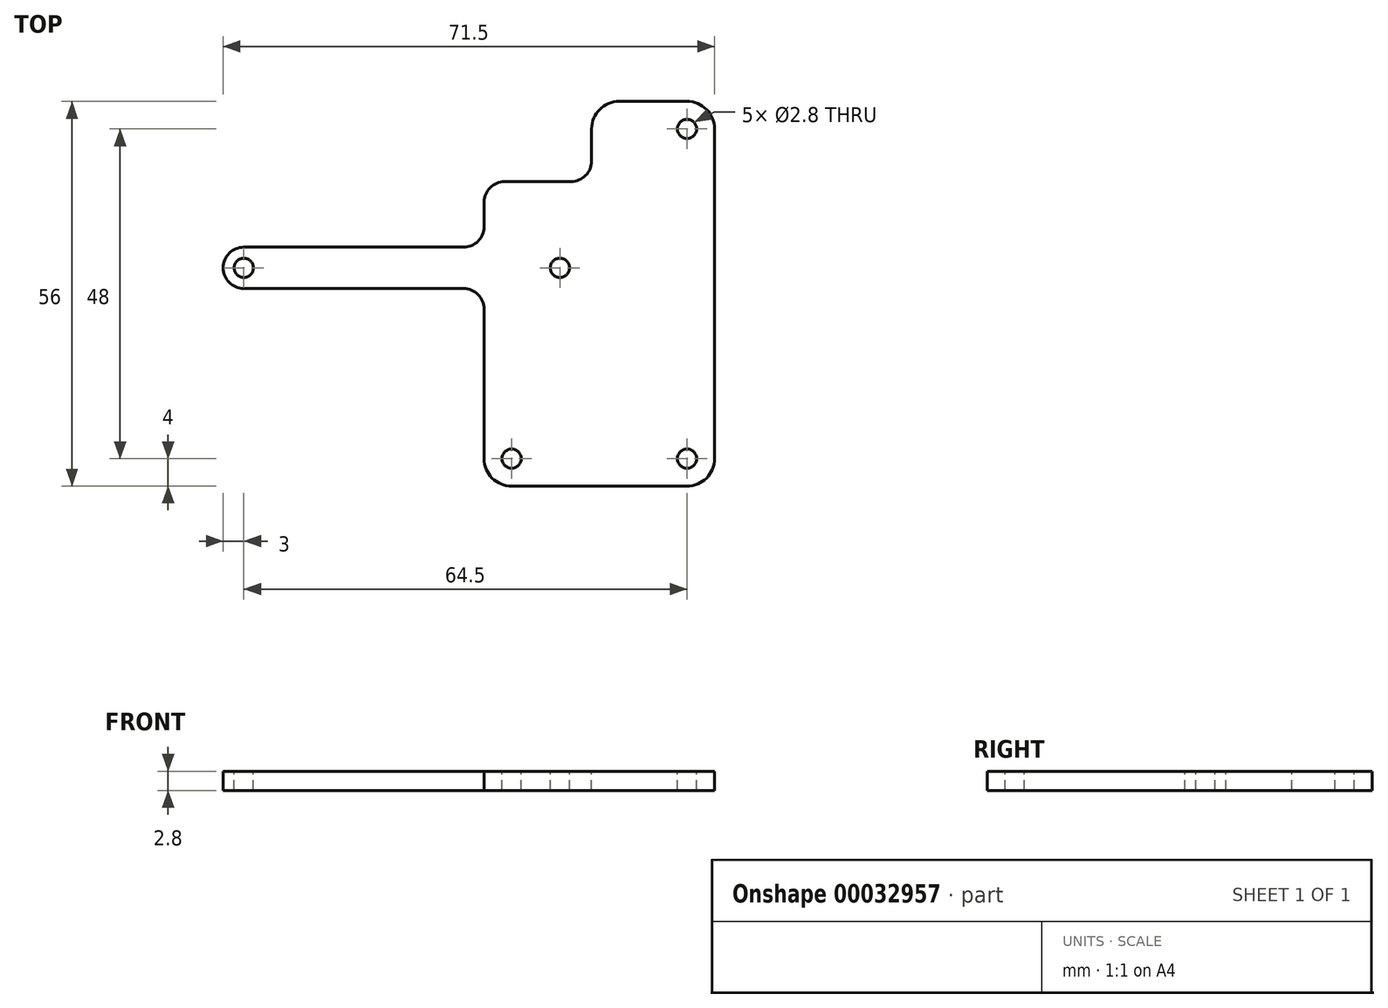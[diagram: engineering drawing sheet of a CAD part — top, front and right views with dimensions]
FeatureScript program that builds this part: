
annotation { "Feature Type Name" : "Feature", "Feature Type Description" : "" }
export const myFeature = defineFeature(function(context is Context, id is Id, definition is map)
    precondition{}
    {
        {
            var Q0;
            Q0=qCreatedBy(makeId("Top.planeOp"),FACE);
            var sketch = newSketch(context, id + "F0", { "sketchPlane" : qUnion([Q0])});
            skLineSegment(sketch, "E0.rect.bottom", {"start": v(5.82, -11.88) * mm, "end": v(-5.83, -11.88) * mm});
            skLineSegment(sketch, "E0.rect.top", {"start": v(5.83, 11.88) * mm, "end": v(-5.82, 11.88) * mm});
            skLineSegment(sketch, "E0.rect.left", {"start": v(5.82, -11.88) * mm, "end": v(5.83, 11.88) * mm});
            skLineSegment(sketch, "E0.rect.right", {"start": v(-5.83, -11.88) * mm, "end": v(-5.82, 11.87) * mm});
            skPoint(sketch, "E0.rect.middle", {"position": v(0, 0) * mm});
            skSolve(sketch);
        }
        {
            var Q0;
            Q0=qSketchRegion(id+"F0",true);
            extrude(context, id + "F1", {"entities" : qUnion([Q0]), "depth" : 20.4 * mm});
        }
        {
            var Q0;
            Q0=makeQuery(id+"F1.opExtrude","CAP_FACE",FACE,{"disambiguationData":[OSD([sQuery(id+"F0.wireOp",EDGE,"E0.rect.bottom"),sQuery(id+"F0.wireOp",EDGE,"E0.rect.top"),sQuery(id+"F0.wireOp",EDGE,"E0.rect.left"),sQuery(id+"F0.wireOp",EDGE,"E0.rect.right")])],"isStart":false});
            var sketch = newSketch(context, id + "F2", { "sketchPlane" : qUnion([Q0])});
            skArc(sketch, "E1", {"start": v(5.83, 7.59) * mm, "mid": v(0, 11.88) * mm, "end": v(-5.83, 7.59) * mm});
            skLineSegment(sketch, "E2", {"start": v(5.83, 7.59) * mm, "end": v(5.83, 3.96) * mm});
            skLineSegment(sketch, "E3.MirrorCS", {"start": v(-5.83, 7.59) * mm, "end": v(-5.83, 3.96) * mm});
            skArc(sketch, "E4.trimOffspring", {"start": v(-5.83, 3.96) * mm, "mid": v(-4.78, 1.98) * mm, "end": v(-3.09, 0.51) * mm});
            skArc(sketch, "E5", {"start": v(-3.09, 0.51) * mm, "mid": v(0, -3.1) * mm, "end": v(3.09, 0.51) * mm});
            skArc(sketch, "E6.trimOffspring", {"start": v(3.09, 0.51) * mm, "mid": v(4.78, 1.98) * mm, "end": v(5.83, 3.96) * mm});
            skSolve(sketch);
        }
        {
            var Q0;
            Q0=qSketchRegion(id+"F2",true);
            extrude(context, id + "F3", {"entities" : qUnion([Q0]), "operationType" : NewBodyOperationType.ADD, "depth" : 6 * mm});
        }
        {
            var Q0;
            {var subQ0=sQuery(id+"F0.wireOp",EDGE,"E0.rect.bottom");var subQ1=sQuery(id+"F0.wireOp",EDGE,"E0.rect.left");var subQ2=sQuery(id+"F0.wireOp",EDGE,"E0.rect.right");Q0=makeQuery(id+"F3.boolean.opBoolean","SPLIT",FACE,{"disambiguationData":[TD([makeQuery(id+"F1.opExtrude","SWEPT_FACE",FACE,{"disambiguationData":[OSD([subQ0])]}),makeQuery(id+"F1.opExtrude","SWEPT_FACE",FACE,{"disambiguationData":[OSD([subQ1])]}),makeQuery(id+"F1.opExtrude","SWEPT_FACE",FACE,{"disambiguationData":[OSD([subQ2])]}),makeQuery(id+"F3.opExtrude","SWEPT_FACE",FACE,{"disambiguationData":[OSD([sQuery(id+"F2.wireOp",EDGE,"E2")])]}),makeQuery(id+"F3.opExtrude","SWEPT_FACE",FACE,{"disambiguationData":[OSD([sQuery(id+"F2.wireOp",EDGE,"E3.MirrorCS")])]}),makeQuery(id+"F3.opExtrude","SWEPT_FACE",FACE,{"disambiguationData":[OSD([sQuery(id+"F2.wireOp",EDGE,"E4.trimOffspring")])]}),makeQuery(id+"F3.opExtrude","SWEPT_FACE",FACE,{"disambiguationData":[OSD([sQuery(id+"F2.wireOp",EDGE,"E5")])]}),makeQuery(id+"F3.opExtrude","SWEPT_FACE",FACE,{"disambiguationData":[OSD([sQuery(id+"F2.wireOp",EDGE,"E6.trimOffspring")])]})])],"derivedFrom":makeQuery(id+"F1.opExtrude","CAP_FACE",FACE,{"disambiguationData":[OSD([subQ0,sQuery(id+"F0.wireOp",EDGE,"E0.rect.top"),subQ1,subQ2])],"isStart":false})});}
            var sketch = newSketch(context, id + "F4", { "sketchPlane" : qUnion([Q0])});
            skLineSegment(sketch, "E7.bottom", {"start": v(-5.83, -11.88) * mm, "end": v(5.82, -11.88) * mm});
            skLineSegment(sketch, "E7.top", {"start": v(-5.83, -16.08) * mm, "end": v(5.82, -16.08) * mm});
            skLineSegment(sketch, "E7.left", {"start": v(-5.83, -11.88) * mm, "end": v(-5.83, -16.08) * mm});
            skLineSegment(sketch, "E7.right", {"start": v(5.82, -11.88) * mm, "end": v(5.82, -16.08) * mm});
            skLineSegment(sketch, "E8.MirrorCS", {"start": v(-5.83, 11.88) * mm, "end": v(-5.83, 16.08) * mm});
            skLineSegment(sketch, "E9.MirrorCS", {"start": v(-5.83, 16.08) * mm, "end": v(5.82, 16.08) * mm});
            skLineSegment(sketch, "E10.MirrorCS", {"start": v(5.82, 11.88) * mm, "end": v(5.82, 16.08) * mm});
            skLineSegment(sketch, "E11.MirrorCS", {"start": v(-5.83, 11.88) * mm, "end": v(5.82, 11.88) * mm});
            skSolve(sketch);
        }
        {
            var Q0;
            Q0=makeQuery(id+"F4.imprint","IMPRINT",FACE,{"disambiguationData":[TD([[makeQuery(id+"F4.imprint","IMPRINT",EDGE,{"derivedFrom":sQuery(id+"F4.wireOp",EDGE,"E7.bottom")}),1.0]])]});
            var Q1;
            Q1=makeQuery(id+"F4.imprint","IMPRINT",FACE,{"disambiguationData":[TD([[makeQuery(id+"F4.imprint","IMPRINT",EDGE,{"derivedFrom":sQuery(id+"F4.wireOp",EDGE,"E8.MirrorCS")}),-1.0]])]});
            extrude(context, id + "F5", {"entities" : qUnion([Q0, Q1]), "operationType" : NewBodyOperationType.ADD, "oppositeDirection" : true, "depth" : 2.8 * mm, "hasSecondDirection" : true, "secondDirectionOppositeDirection" : true, "secondDirectionDepth" : .8 * mm});
        }
        {
            var Q0;
            {var subQ0=sQuery(id+"F0.wireOp",EDGE,"E0.rect.top");var subQ1=sQuery(id+"F0.wireOp",EDGE,"E0.rect.left");Q0=makeQuery(id+"F5.boolean.opBoolean","SPLIT",EDGE,{"disambiguationData":[TD([makeQuery(id+"F1.opExtrude","CAP_FACE",FACE,{"disambiguationData":[OSD([sQuery(id+"F0.wireOp",EDGE,"E0.rect.bottom"),subQ0,subQ1,sQuery(id+"F0.wireOp",EDGE,"E0.rect.right")])],"isStart":true})])],"derivedFrom":makeQuery(id+"F1.opExtrude","SWEPT_EDGE",EDGE,{"disambiguationData":[OSD([subQ0,subQ1])]})});}
            var Q1;
            {var subQ0=sQuery(id+"F0.wireOp",EDGE,"E0.rect.bottom");var subQ1=sQuery(id+"F0.wireOp",EDGE,"E0.rect.left");Q1=makeQuery(id+"F5.boolean.opBoolean","SPLIT",EDGE,{"disambiguationData":[TD([makeQuery(id+"F1.opExtrude","CAP_FACE",FACE,{"disambiguationData":[OSD([subQ0,sQuery(id+"F0.wireOp",EDGE,"E0.rect.top"),subQ1,sQuery(id+"F0.wireOp",EDGE,"E0.rect.right")])],"isStart":true})])],"derivedFrom":makeQuery(id+"F1.opExtrude","SWEPT_EDGE",EDGE,{"disambiguationData":[OSD([subQ0,subQ1])]})});}
            var Q2;
            {var subQ0=sQuery(id+"F0.wireOp",EDGE,"E0.rect.bottom");var subQ1=sQuery(id+"F0.wireOp",EDGE,"E0.rect.right");Q2=makeQuery(id+"F5.boolean.opBoolean","SPLIT",EDGE,{"disambiguationData":[TD([makeQuery(id+"F1.opExtrude","CAP_FACE",FACE,{"disambiguationData":[OSD([subQ0,sQuery(id+"F0.wireOp",EDGE,"E0.rect.top"),sQuery(id+"F0.wireOp",EDGE,"E0.rect.left"),subQ1])],"isStart":true})])],"derivedFrom":makeQuery(id+"F1.opExtrude","SWEPT_EDGE",EDGE,{"disambiguationData":[OSD([subQ0,subQ1])]})});}
            var Q3;
            {var subQ0=sQuery(id+"F0.wireOp",EDGE,"E0.rect.top");var subQ1=sQuery(id+"F0.wireOp",EDGE,"E0.rect.right");Q3=makeQuery(id+"F5.boolean.opBoolean","SPLIT",EDGE,{"disambiguationData":[TD([makeQuery(id+"F1.opExtrude","CAP_FACE",FACE,{"disambiguationData":[OSD([sQuery(id+"F0.wireOp",EDGE,"E0.rect.bottom"),subQ0,sQuery(id+"F0.wireOp",EDGE,"E0.rect.left"),subQ1])],"isStart":true})])],"derivedFrom":makeQuery(id+"F1.opExtrude","SWEPT_EDGE",EDGE,{"disambiguationData":[OSD([subQ0,subQ1])]})});}
            fillet(context, id + "F6", {"entities" : qUnion([Q0, Q1, Q2, Q3]), "radius" : .5 * mm, "tangentPropagation" : true, "allowEdgeOverflow" : false});
        }
        {
            var Q0;
            Q0=makeQuery(id+"F5.opExtrude","SWEPT_EDGE",EDGE,{"disambiguationData":[OSD([sQuery(id+"F4.wireOp",EDGE,"E8.MirrorCS"),sQuery(id+"F4.wireOp",EDGE,"E9.MirrorCS")])]});
            var Q1;
            Q1=makeQuery(id+"F5.opExtrude","SWEPT_EDGE",EDGE,{"disambiguationData":[OSD([sQuery(id+"F4.wireOp",EDGE,"E9.MirrorCS"),sQuery(id+"F4.wireOp",EDGE,"E10.MirrorCS")])]});
            var Q2;
            Q2=makeQuery(id+"F5.opExtrude","SWEPT_EDGE",EDGE,{"disambiguationData":[OSD([sQuery(id+"F4.wireOp",EDGE,"E7.top"),sQuery(id+"F4.wireOp",EDGE,"E7.right")])]});
            var Q3;
            Q3=makeQuery(id+"F5.opExtrude","SWEPT_EDGE",EDGE,{"disambiguationData":[OSD([sQuery(id+"F4.wireOp",EDGE,"E7.top"),sQuery(id+"F4.wireOp",EDGE,"E7.left")])]});
            fillet(context, id + "F7", {"entities" : qUnion([Q0, Q1, Q2, Q3]), "radius" : 1 * mm, "tangentPropagation" : true, "allowEdgeOverflow" : false});
        }
        {
            var Q0;
            Q0=makeQuery(id+"F3.opExtrude","CAP_FACE",FACE,{"disambiguationData":[OSD([sQuery(id+"F2.wireOp",EDGE,"E1"),sQuery(id+"F2.wireOp",EDGE,"E2"),sQuery(id+"F2.wireOp",EDGE,"E3.MirrorCS"),sQuery(id+"F2.wireOp",EDGE,"E4.trimOffspring"),sQuery(id+"F2.wireOp",EDGE,"E5"),sQuery(id+"F2.wireOp",EDGE,"E6.trimOffspring")])],"isStart":false});
            var sketch = newSketch(context, id + "F8", { "sketchPlane" : qUnion([Q0])});
            skLineSegment(sketch, "E12", {"start": v(-5.83, 3.96) * mm, "end": v(-5.83, 5.78) * mm});
            skLineSegment(sketch, "E13.rect.bottom", {"start": v(22.5, 30) * mm, "end": v(4.61, 30) * mm});
            skLineSegment(sketch, "E13.rect.left", {"start": v(22.5, 30) * mm, "end": v(22.5, -26) * mm});
            skPoint(sketch, "E13.rect.middle", {"position": v(0, 0) * mm});
            skCircle(sketch, "E14.MirrorC", {"center": v(18.5, 26) * mm, "radius": 1.4 * mm});
            skLineSegment(sketch, "E15", {"start": v(4.61, 30) * mm, "end": v(4.61, 21.32) * mm});
            skLineSegment(sketch, "E16", {"start": v(1.61, 18.32) * mm, "end": v(-8.03, 18.32) * mm});
            skLineSegment(sketch, "E17", {"start": v(-11.03, 15.32) * mm, "end": v(-11.03, 11.78) * mm});
            skPoint(sketch, "E18.orphan", {"position": v(-22.5, 30) * mm});
            skPoint(sketch, "E19.visualSharp", {"position": v(-11.03, -26) * mm});
            skPoint(sketch, "E20.visualSharp", {"position": v(4.61, 18.32) * mm});
            skArc(sketch, "E20.filletArc", {"start": v(1.61, 18.32) * mm, "mid": v(3.73, 19.2) * mm, "end": v(4.61, 21.32) * mm});
            skPoint(sketch, "E21.visualSharp", {"position": v(-11.03, 18.32) * mm});
            skArc(sketch, "E21.filletArc", {"start": v(-8.03, 18.32) * mm, "mid": v(-10.15, 17.44) * mm, "end": v(-11.03, 15.32) * mm});
            skLineSegment(sketch, "E22", {"start": v(0, 5.78) * mm, "end": v(-46, 5.78) * mm, "construction": true});
            skCircle(sketch, "E23", {"center": v(-46, 5.78) * mm, "radius": 1.4 * mm});
            skArc(sketch, "E24", {"start": v(-46, 8.78) * mm, "mid": v(-49, 5.78) * mm, "end": v(-46, 2.78) * mm});
            skLineSegment(sketch, "E25", {"start": v(-46, 2.78) * mm, "end": v(-14.03, 2.78) * mm});
            skLineSegment(sketch, "E26.MirrorCS", {"start": v(-46, 8.78) * mm, "end": v(-14.03, 8.78) * mm});
            skLineSegment(sketch, "E27.trimOffspring", {"start": v(-11.03, -0.22) * mm, "end": v(-11.03, -15.07) * mm});
            skPoint(sketch, "E28.visualSharp", {"position": v(-11.03, 8.78) * mm});
            skArc(sketch, "E28.filletArc", {"start": v(-14.03, 8.78) * mm, "mid": v(-11.9, 9.65) * mm, "end": v(-11.03, 11.78) * mm});
            skPoint(sketch, "E29.visualSharp", {"position": v(-11.03, 2.78) * mm});
            skArc(sketch, "E29.filletArc", {"start": v(-11.03, -0.22) * mm, "mid": v(-11.9, 1.9) * mm, "end": v(-14.03, 2.77) * mm});
            skLineSegment(sketch, "E30", {"start": v(-11.03, -15.07) * mm, "end": v(-11.03, -26) * mm});
            skLineSegment(sketch, "E31", {"start": v(-11.03, -26) * mm, "end": v(22.5, -26) * mm});
            skLineSegment(sketch, "E32.bottom", {"start": v(-11.03, -26) * mm, "end": v(-7.03, -26) * mm, "construction": true});
            skLineSegment(sketch, "E32.top", {"start": v(-11.03, -22) * mm, "end": v(-7.03, -22) * mm, "construction": true});
            skLineSegment(sketch, "E32.left", {"start": v(-11.03, -26) * mm, "end": v(-11.03, -22) * mm, "construction": true});
            skLineSegment(sketch, "E32.right", {"start": v(-7.03, -26) * mm, "end": v(-7.03, -22) * mm, "construction": true});
            skCircle(sketch, "E33", {"center": v(-7.03, -22) * mm, "radius": 1.4 * mm});
            skLineSegment(sketch, "E34.bottom", {"start": v(22.5, -26) * mm, "end": v(18.5, -26) * mm, "construction": true});
            skLineSegment(sketch, "E34.top", {"start": v(22.5, -22) * mm, "end": v(18.5, -22) * mm, "construction": true});
            skLineSegment(sketch, "E34.left", {"start": v(22.5, -26) * mm, "end": v(22.5, -22) * mm, "construction": true});
            skLineSegment(sketch, "E34.right", {"start": v(18.5, -26) * mm, "end": v(18.5, -22) * mm, "construction": true});
            skCircle(sketch, "E35", {"center": v(18.5, -22) * mm, "radius": 1.4 * mm});
            skCircle(sketch, "E36", {"center": v(0, 5.78) * mm, "radius": 1.4 * mm});
            skPoint(sketch, "E37.orphan", {"position": v(-5.83, 7.59) * mm});
            skPoint(sketch, "E38.MirrorCS.end.orphan", {"position": v(5.83, 7.59) * mm});
            skPoint(sketch, "E39.end.orphan", {"position": v(5.83, 3.96) * mm});
            skSolve(sketch);
        }
        {
            var Q0;
            Q0=qSketchRegion(id+"F8",true);
            extrude(context, id + "F9", {"entities" : qUnion([Q0]), "oppositeDirection" : true, "depth" : 2.8 * mm});
        }
        {
            var Q0;
            Q0=makeQuery(id+"F9.opExtrude","SWEPT_EDGE",EDGE,{"disambiguationData":[OSD([sQuery(id+"F8.wireOp",EDGE,"E13.rect.top"),sQuery(id+"F8.wireOp",EDGE,"E13.rect.right")])]});
            var Q1;
            Q1=makeQuery(id+"F9.opExtrude","SWEPT_EDGE",EDGE,{"disambiguationData":[OSD([sQuery(id+"F8.wireOp",EDGE,"E13.rect.bottom"),sQuery(id+"F8.wireOp",EDGE,"E13.rect.right")])]});
            var Q2;
            Q2=makeQuery(id+"F9.opExtrude","SWEPT_EDGE",EDGE,{"disambiguationData":[OSD([sQuery(id+"F8.wireOp",EDGE,"E13.rect.bottom"),sQuery(id+"F8.wireOp",EDGE,"E13.rect.left")])]});
            var Q3;
            Q3=makeQuery(id+"F9.opExtrude","SWEPT_EDGE",EDGE,{"disambiguationData":[OSD([sQuery(id+"F8.wireOp",EDGE,"E13.rect.top"),sQuery(id+"F8.wireOp",EDGE,"E13.rect.left")])]});
            var Q4;
            Q4=makeQuery(id+"F9.opExtrude","SWEPT_EDGE",EDGE,{"disambiguationData":[OSD([sQuery(id+"F8.wireOp",EDGE,"E30"),sQuery(id+"F8.wireOp",EDGE,"E31")])]});
            fillet(context, id + "F10", {"entities" : qUnion([Q0, Q1, Q2, Q3, Q4]), "radius" : 4 * mm, "tangentPropagation" : true, "allowEdgeOverflow" : false});
        }
        {
            var Q0;
            Q0=makeQuery(id+"F9.opExtrude","SWEPT_BODY",BODY,{"disambiguationData":[OSD([sQuery(id+"F8.wireOp",EDGE,"E39"),sQuery(id+"F8.wireOp",EDGE,"a7b3f6ed-c376-49eb-9cb2-135e59594782"),sQuery(id+"F8.wireOp",EDGE,"E12"),sQuery(id+"F8.wireOp",EDGE,"E38.MirrorCS"),sQuery(id+"F8.wireOp",EDGE,"d2d63f77-5541-4a7f-8d51-7ca97668e1f1.trimOffspring"),sQuery(id+"F8.wireOp",EDGE,"b199d975-cfa0-4d79-aa76-c9a82bb31a59.trimOffspring"),sQuery(id+"F8.wireOp",EDGE,"E13.rect.bottom"),sQuery(id+"F8.wireOp",EDGE,"E13.rect.top"),sQuery(id+"F8.wireOp",EDGE,"E13.rect.left"),sQuery(id+"F8.wireOp",EDGE,"E13.rect.right"),sQuery(id+"F8.wireOp",EDGE,"a12ce330-09d9-461c-8b2f-e163017ed208"),sQuery(id+"F8.wireOp",EDGE,"ce85554a-ae08-408d-bbdd-004999f886530.MirrorC"),sQuery(id+"F8.wireOp",EDGE,"74581e88-93ef-4e49-bf24-ccc966527bf30.MirrorC"),sQuery(id+"F8.wireOp",EDGE,"E14.MirrorC"),sQuery(id+"F8.wireOp",EDGE,"76930b9b-8da1-4d4d-b0e5-4a7641f42912"),sQuery(id+"F8.wireOp",EDGE,"f42893a9-d5a1-4c2e-96db-01520e8eb7290.MirrorC"),sQuery(id+"F8.wireOp",EDGE,"46118b25-6d7d-4224-8583-2d73bb83e9220.MirrorC"),sQuery(id+"F8.wireOp",EDGE,"b2e64fab-b84c-4731-9833-593c73ce0a330.MirrorC")])]});
            transform(context, id + "F11", {"entities" : qUnion([Q0]), "transformType" : TransformType.TRANSLATION_3D, "dx" : 0 * mm, "dy" : 0 * mm, "dz" : 0 * mm, "makeCopy" : true});
        }
        {
            var Q0;
            Q0=makeQuery(id+"F11.opPattern","COPY",BODY,{"derivedFrom":makeQuery(id+"F9.opExtrude","SWEPT_BODY",BODY,{"disambiguationData":[OSD([sQuery(id+"F8.wireOp",EDGE,"E39"),sQuery(id+"F8.wireOp",EDGE,"a7b3f6ed-c376-49eb-9cb2-135e59594782"),sQuery(id+"F8.wireOp",EDGE,"E12"),sQuery(id+"F8.wireOp",EDGE,"E38.MirrorCS"),sQuery(id+"F8.wireOp",EDGE,"d2d63f77-5541-4a7f-8d51-7ca97668e1f1.trimOffspring"),sQuery(id+"F8.wireOp",EDGE,"b199d975-cfa0-4d79-aa76-c9a82bb31a59.trimOffspring"),sQuery(id+"F8.wireOp",EDGE,"E13.rect.bottom"),sQuery(id+"F8.wireOp",EDGE,"E13.rect.top"),sQuery(id+"F8.wireOp",EDGE,"E13.rect.left"),sQuery(id+"F8.wireOp",EDGE,"E13.rect.right"),sQuery(id+"F8.wireOp",EDGE,"a12ce330-09d9-461c-8b2f-e163017ed208"),sQuery(id+"F8.wireOp",EDGE,"74581e88-93ef-4e49-bf24-ccc966527bf30.MirrorC"),sQuery(id+"F8.wireOp",EDGE,"E14.MirrorC"),sQuery(id+"F8.wireOp",EDGE,"76930b9b-8da1-4d4d-b0e5-4a7641f42912"),sQuery(id+"F8.wireOp",EDGE,"f42893a9-d5a1-4c2e-96db-01520e8eb7290.MirrorC"),sQuery(id+"F8.wireOp",EDGE,"b2e64fab-b84c-4731-9833-593c73ce0a330.MirrorC"),sQuery(id+"F8.wireOp",EDGE,"E15"),sQuery(id+"F8.wireOp",EDGE,"E16"),sQuery(id+"F8.wireOp",EDGE,"E17"),sQuery(id+"F8.wireOp",EDGE,"8f80475a-625c-4095-acb9-1eab8cfb7864"),sQuery(id+"F8.wireOp",EDGE,"E19.filletArc"),sQuery(id+"F8.wireOp",EDGE,"E20.filletArc"),sQuery(id+"F8.wireOp",EDGE,"E21.filletArc")])]}),"instanceName":"1"});
            deleteBodies(context, id + "F12", {"entities" : qUnion([Q0])});
        }
        {
            var Q0;
            Q0=makeQuery(id+"F1.opExtrude","SWEPT_BODY",BODY,{"disambiguationData":[OSD([sQuery(id+"F0.wireOp",EDGE,"E0.rect.bottom"),sQuery(id+"F0.wireOp",EDGE,"E0.rect.top"),sQuery(id+"F0.wireOp",EDGE,"E0.rect.left"),sQuery(id+"F0.wireOp",EDGE,"E0.rect.right")])]});
            deleteBodies(context, id + "F13", {"entities" : qUnion([Q0])});
        }
    });
